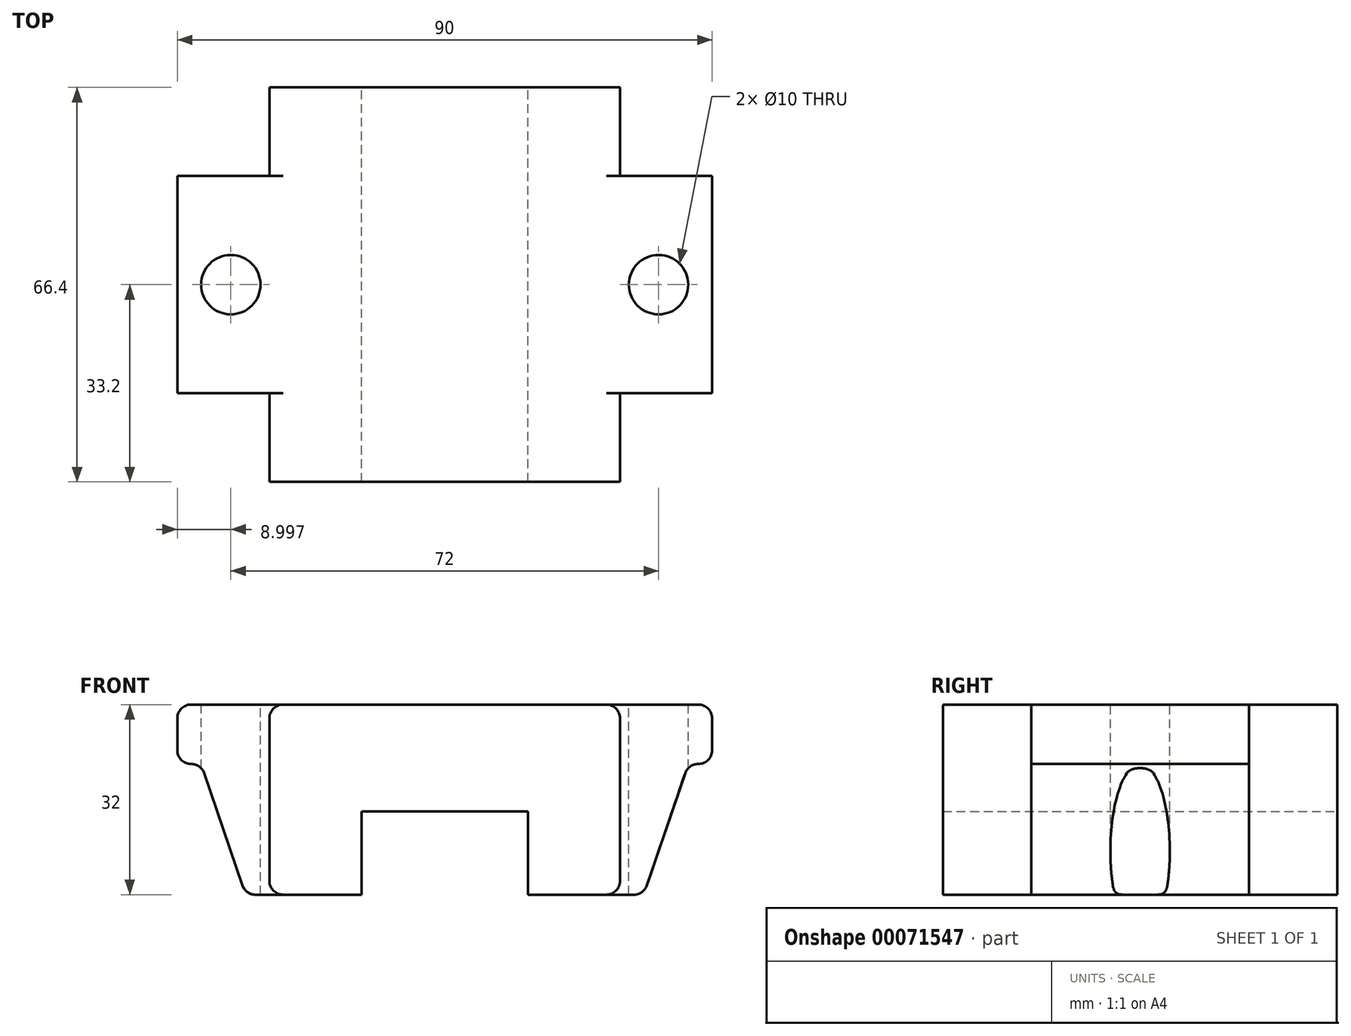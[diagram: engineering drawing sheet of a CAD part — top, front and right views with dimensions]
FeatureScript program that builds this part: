
annotation { "Feature Type Name" : "Feature", "Feature Type Description" : "" }
export const myFeature = defineFeature(function(context is Context, id is Id, definition is map)
    precondition{}
    {
        {
            var Q0;
            Q0=qCreatedBy(makeId("Front.planeOp"),FACE);
            var sketch = newSketch(context, id + "F0", { "sketchPlane" : qUnion([Q0])});
            skLineSegment(sketch, "E0.bottom", {"start": v(-43.91, 8.76) * mm, "end": v(46.09, 8.76) * mm});
            skLineSegment(sketch, "E0.top", {"start": v(-32.41, -23.24) * mm, "end": v(-12.91, -23.24) * mm});
            skLineSegment(sketch, "E0.left", {"start": v(-43.91, 8.76) * mm, "end": v(-43.91, -1.24) * mm});
            skLineSegment(sketch, "E0.right", {"start": v(46.09, 8.76) * mm, "end": v(46.09, -1.24) * mm});
            skLineSegment(sketch, "E1.top", {"start": v(-43.91, -1.24) * mm, "end": v(-39.91, -1.24) * mm});
            skLineSegment(sketch, "E2.bottom", {"start": v(-28.41, 8.76) * mm, "end": v(30.59, 8.76) * mm});
            skLineSegment(sketch, "E2.top", {"start": v(-28.41, -23.24) * mm, "end": v(-12.91, -23.24) * mm});
            skLineSegment(sketch, "E2.left", {"start": v(-28.41, 8.76) * mm, "end": v(-28.41, -23.24) * mm});
            skLineSegment(sketch, "E2.right", {"start": v(30.59, 8.76) * mm, "end": v(30.59, -23.24) * mm});
            skLineSegment(sketch, "E3.top", {"start": v(-12.91, -9.24) * mm, "end": v(15.09, -9.24) * mm});
            skLineSegment(sketch, "E3.left", {"start": v(-12.91, -23.24) * mm, "end": v(-12.91, -9.24) * mm});
            skLineSegment(sketch, "E3.right", {"start": v(15.09, -23.24) * mm, "end": v(15.09, -9.24) * mm});
            skLineSegment(sketch, "E4.trimOffspring", {"start": v(15.09, -23.24) * mm, "end": v(30.59, -23.24) * mm});
            skLineSegment(sketch, "E5.trimOffspring", {"start": v(15.09, -23.24) * mm, "end": v(34.59, -23.24) * mm});
            skLineSegment(sketch, "E6", {"start": v(-39.91, -1.24) * mm, "end": v(-32.41, -23.24) * mm});
            skLineSegment(sketch, "E7", {"start": v(34.59, -23.24) * mm, "end": v(42.09, -1.24) * mm});
            skLineSegment(sketch, "E8.trimOffspring", {"start": v(42.09, -1.24) * mm, "end": v(46.09, -1.24) * mm});
            skSolve(sketch);
        }
        {
            var Q0;
            Q0=qSketchRegion(id+"F0",true);
            extrude(context, id + "F1", {"entities" : qUnion([Q0]), "depth" : 36.6 * mm});
        }
        {
            var Q0;
            Q0=makeQuery(id+"F1.opExtrude","CAP_FACE",FACE,{"disambiguationData":[OSD([sQuery(id+"F0.wireOp",EDGE,"E0.top"),sQuery(id+"F0.wireOp",EDGE,"E0.bottom"),sQuery(id+"F0.wireOp",EDGE,"E1.top"),sQuery(id+"F0.wireOp",EDGE,"E0.left"),sQuery(id+"F0.wireOp",EDGE,"E0.right"),sQuery(id+"F0.wireOp",EDGE,"E2.bottom"),sQuery(id+"F0.wireOp",EDGE,"E2.top"),sQuery(id+"F0.wireOp",EDGE,"E3.top"),sQuery(id+"F0.wireOp",EDGE,"E3.left"),sQuery(id+"F0.wireOp",EDGE,"E3.right"),sQuery(id+"F0.wireOp",EDGE,"E5.trimOffspring"),sQuery(id+"F0.wireOp",EDGE,"E6"),sQuery(id+"F0.wireOp",EDGE,"E7"),sQuery(id+"F0.wireOp",EDGE,"E8.trimOffspring")])],"isStart":true});
            var sketch = newSketch(context, id + "F2", { "sketchPlane" : qUnion([Q0])});
            skLineSegment(sketch, "E9.top", {"start": v(-30.59, 8.76) * mm, "end": v(28.41, 8.76) * mm});
            skLineSegment(sketch, "E9.left", {"start": v(-30.59, -23.24) * mm, "end": v(-30.59, 8.76) * mm});
            skLineSegment(sketch, "E9.right", {"start": v(28.41, -23.24) * mm, "end": v(28.41, 8.76) * mm});
            skLineSegment(sketch, "E10.top", {"start": v(-15.09, -9.24) * mm, "end": v(12.91, -9.24) * mm});
            skLineSegment(sketch, "E10.left", {"start": v(-15.09, -23.24) * mm, "end": v(-15.09, -9.24) * mm});
            skLineSegment(sketch, "E10.right", {"start": v(12.91, -23.24) * mm, "end": v(12.91, -9.24) * mm});
            skLineSegment(sketch, "E11.trimOffspring", {"start": v(12.91, -23.24) * mm, "end": v(28.41, -23.24) * mm});
            skLineSegment(sketch, "E12", {"start": v(-30.59, -23.24) * mm, "end": v(-15.09, -23.24) * mm});
            skSolve(sketch);
        }
        {
            var Q0;
            Q0=qSketchRegion(id+"F2",true);
            extrude(context, id + "F3", {"entities" : qUnion([Q0]), "operationType" : NewBodyOperationType.ADD, "depth" : 14.9 * mm, "hasSecondDirection" : true, "secondDirectionOppositeDirection" : true, "secondDirectionDepth" : 51.5 * mm});
        }
        {
            var Q0;
            Q0=makeQuery(id+"F3.boolean.opBoolean","MERGE",FACE,{"derivedFrom":[makeQuery(id+"F1.opExtrude","SWEPT_FACE",FACE,{"disambiguationData":[OSD([sQuery(id+"F0.wireOp",EDGE,"E0.bottom"),sQuery(id+"F0.wireOp",EDGE,"E2.bottom")])]}),makeQuery(id+"F3.opExtrude","SWEPT_FACE",FACE,{"disambiguationData":[OSD([sQuery(id+"F2.wireOp",EDGE,"E9.top")])]})]});
            var sketch = newSketch(context, id + "F4", { "sketchPlane" : qUnion([Q0])});
            skCircle(sketch, "E13", {"center": v(-34.91, -18.3) * mm, "radius": 5 * mm});
            skCircle(sketch, "E14", {"center": v(37.09, -18.3) * mm, "radius": 5 * mm});
            skSolve(sketch);
        }
        {
            var Q0;
            Q0=qSketchRegion(id+"F4",true);
            extrude(context, id + "F5", {"entities" : qUnion([Q0]), "operationType" : NewBodyOperationType.REMOVE, "endBound" : BoundingType.THROUGH_ALL, "oppositeDirection" : true, "depth" : 25 * mm});
        }
        {
            var Q0;
            {var subQ0=sQuery(id+"F0.wireOp",EDGE,"E6");var subQ1=sQuery(id+"F0.wireOp",EDGE,"E1.top");Q0=makeQuery(id+"F5.boolean.opBoolean","SPLIT",EDGE,{"disambiguationData":[TD([makeQuery(id+"F1.opExtrude","CAP_FACE",FACE,{"disambiguationData":[OSD([sQuery(id+"F0.wireOp",EDGE,"E0.top"),sQuery(id+"F0.wireOp",EDGE,"E0.bottom"),subQ1,sQuery(id+"F0.wireOp",EDGE,"E0.left"),sQuery(id+"F0.wireOp",EDGE,"E0.right"),sQuery(id+"F0.wireOp",EDGE,"E2.bottom"),sQuery(id+"F0.wireOp",EDGE,"E2.top"),sQuery(id+"F0.wireOp",EDGE,"E3.top"),sQuery(id+"F0.wireOp",EDGE,"E3.left"),sQuery(id+"F0.wireOp",EDGE,"E3.right"),sQuery(id+"F0.wireOp",EDGE,"E5.trimOffspring"),subQ0,sQuery(id+"F0.wireOp",EDGE,"E7"),sQuery(id+"F0.wireOp",EDGE,"E8.trimOffspring")])],"isStart":false})])],"derivedFrom":makeQuery(id+"F1.opExtrude","SWEPT_EDGE",EDGE,{"disambiguationData":[OSD([subQ1,subQ0])]})});}
            var Q1;
            Q1=makeQuery(id+"F1.opExtrude","SWEPT_EDGE",EDGE,{"disambiguationData":[OSD([sQuery(id+"F0.wireOp",EDGE,"E1.top"),sQuery(id+"F0.wireOp",EDGE,"E0.left")])]});
            var Q2;
            Q2=makeQuery(id+"F1.opExtrude","SWEPT_EDGE",EDGE,{"disambiguationData":[OSD([sQuery(id+"F0.wireOp",EDGE,"E0.bottom"),sQuery(id+"F0.wireOp",EDGE,"E0.left")])]});
            var Q3;
            {var subQ0=sQuery(id+"F0.wireOp",EDGE,"E6");var subQ1=sQuery(id+"F0.wireOp",EDGE,"E2.top");var subQ2=sQuery(id+"F0.wireOp",EDGE,"E0.top");Q3=makeQuery(id+"F5.boolean.opBoolean","SPLIT",EDGE,{"disambiguationData":[TD([makeQuery(id+"F1.opExtrude","CAP_FACE",FACE,{"disambiguationData":[OSD([subQ2,sQuery(id+"F0.wireOp",EDGE,"E0.bottom"),sQuery(id+"F0.wireOp",EDGE,"E1.top"),sQuery(id+"F0.wireOp",EDGE,"E0.left"),sQuery(id+"F0.wireOp",EDGE,"E0.right"),sQuery(id+"F0.wireOp",EDGE,"E2.bottom"),subQ1,sQuery(id+"F0.wireOp",EDGE,"E3.top"),sQuery(id+"F0.wireOp",EDGE,"E3.left"),sQuery(id+"F0.wireOp",EDGE,"E3.right"),sQuery(id+"F0.wireOp",EDGE,"E5.trimOffspring"),subQ0,sQuery(id+"F0.wireOp",EDGE,"E7"),sQuery(id+"F0.wireOp",EDGE,"E8.trimOffspring")])],"isStart":false})])],"derivedFrom":makeQuery(id+"F1.opExtrude","SWEPT_EDGE",EDGE,{"disambiguationData":[OSD([subQ2,subQ0])]})});}
            var Q4;
            {var subQ0=sQuery(id+"F0.wireOp",EDGE,"E6");var subQ1=sQuery(id+"F0.wireOp",EDGE,"E2.top");var subQ2=sQuery(id+"F0.wireOp",EDGE,"E0.top");Q4=makeQuery(id+"F5.boolean.opBoolean","SPLIT",EDGE,{"disambiguationData":[TD([makeQuery(id+"F1.opExtrude","CAP_FACE",FACE,{"disambiguationData":[OSD([subQ2,sQuery(id+"F0.wireOp",EDGE,"E0.bottom"),sQuery(id+"F0.wireOp",EDGE,"E1.top"),sQuery(id+"F0.wireOp",EDGE,"E0.left"),sQuery(id+"F0.wireOp",EDGE,"E0.right"),sQuery(id+"F0.wireOp",EDGE,"E2.bottom"),subQ1,sQuery(id+"F0.wireOp",EDGE,"E3.top"),sQuery(id+"F0.wireOp",EDGE,"E3.left"),sQuery(id+"F0.wireOp",EDGE,"E3.right"),sQuery(id+"F0.wireOp",EDGE,"E5.trimOffspring"),subQ0,sQuery(id+"F0.wireOp",EDGE,"E7"),sQuery(id+"F0.wireOp",EDGE,"E8.trimOffspring")])],"isStart":true})])],"derivedFrom":makeQuery(id+"F1.opExtrude","SWEPT_EDGE",EDGE,{"disambiguationData":[OSD([subQ2,subQ0])]})});}
            var Q5;
            {var subQ0=sQuery(id+"F2.wireOp",EDGE,"E9.right");var subQ1=sQuery(id+"F0.wireOp",EDGE,"E2.top");var subQ2=sQuery(id+"F0.wireOp",EDGE,"E0.top");var subQ3=sQuery(id+"F2.wireOp",EDGE,"E11.trimOffspring");Q5=makeQuery(id+"F3.boolean.opBoolean","SPLIT",EDGE,{"disambiguationData":[TD([makeQuery(id+"F3.opExtrude","CAP_FACE",FACE,{"disambiguationData":[OSD([sQuery(id+"F2.wireOp",EDGE,"E9.top"),sQuery(id+"F2.wireOp",EDGE,"E9.left"),subQ0,sQuery(id+"F2.wireOp",EDGE,"E10.top"),sQuery(id+"F2.wireOp",EDGE,"E10.left"),sQuery(id+"F2.wireOp",EDGE,"E10.right"),subQ3,sQuery(id+"F2.wireOp",EDGE,"E12")])],"isStart":true})])],"derivedFrom":makeQuery(id+"F3.opExtrude","SWEPT_EDGE",EDGE,{"disambiguationData":[OSD([subQ2,subQ1,subQ0,subQ3])]})});}
            var Q6;
            {var subQ0=sQuery(id+"F2.wireOp",EDGE,"E9.right");var subQ1=sQuery(id+"F0.wireOp",EDGE,"E2.top");var subQ2=sQuery(id+"F0.wireOp",EDGE,"E0.top");var subQ3=sQuery(id+"F2.wireOp",EDGE,"E11.trimOffspring");Q6=makeQuery(id+"F3.boolean.opBoolean","SPLIT",EDGE,{"disambiguationData":[TD([makeQuery(id+"F3.opExtrude","CAP_FACE",FACE,{"disambiguationData":[OSD([sQuery(id+"F2.wireOp",EDGE,"E9.top"),sQuery(id+"F2.wireOp",EDGE,"E9.left"),subQ0,sQuery(id+"F2.wireOp",EDGE,"E10.top"),sQuery(id+"F2.wireOp",EDGE,"E10.left"),sQuery(id+"F2.wireOp",EDGE,"E10.right"),subQ3,sQuery(id+"F2.wireOp",EDGE,"E12")])],"isStart":false})])],"derivedFrom":makeQuery(id+"F3.opExtrude","SWEPT_EDGE",EDGE,{"disambiguationData":[OSD([subQ2,subQ1,subQ0,subQ3])]})});}
            var Q7;
            {var subQ0=sQuery(id+"F0.wireOp",EDGE,"E2.bottom");var subQ1=sQuery(id+"F0.wireOp",EDGE,"E0.bottom");var subQ2=sQuery(id+"F2.wireOp",EDGE,"E9.right");var subQ3=sQuery(id+"F2.wireOp",EDGE,"E9.top");Q7=makeQuery(id+"F3.boolean.opBoolean","SPLIT",EDGE,{"disambiguationData":[TD([makeQuery(id+"F3.opExtrude","CAP_FACE",FACE,{"disambiguationData":[OSD([subQ3,sQuery(id+"F2.wireOp",EDGE,"E9.left"),subQ2,sQuery(id+"F2.wireOp",EDGE,"E10.top"),sQuery(id+"F2.wireOp",EDGE,"E10.left"),sQuery(id+"F2.wireOp",EDGE,"E10.right"),sQuery(id+"F2.wireOp",EDGE,"E11.trimOffspring"),sQuery(id+"F2.wireOp",EDGE,"E12")])],"isStart":true})])],"derivedFrom":makeQuery(id+"F3.opExtrude","SWEPT_EDGE",EDGE,{"disambiguationData":[OSD([subQ1,subQ0,subQ3,subQ2])]})});}
            var Q8;
            {var subQ0=sQuery(id+"F0.wireOp",EDGE,"E2.bottom");var subQ1=sQuery(id+"F0.wireOp",EDGE,"E0.bottom");var subQ2=sQuery(id+"F2.wireOp",EDGE,"E9.right");var subQ3=sQuery(id+"F2.wireOp",EDGE,"E9.top");Q8=makeQuery(id+"F3.boolean.opBoolean","SPLIT",EDGE,{"disambiguationData":[TD([makeQuery(id+"F3.opExtrude","CAP_FACE",FACE,{"disambiguationData":[OSD([subQ3,sQuery(id+"F2.wireOp",EDGE,"E9.left"),subQ2,sQuery(id+"F2.wireOp",EDGE,"E10.top"),sQuery(id+"F2.wireOp",EDGE,"E10.left"),sQuery(id+"F2.wireOp",EDGE,"E10.right"),sQuery(id+"F2.wireOp",EDGE,"E11.trimOffspring"),sQuery(id+"F2.wireOp",EDGE,"E12")])],"isStart":false})])],"derivedFrom":makeQuery(id+"F3.opExtrude","SWEPT_EDGE",EDGE,{"disambiguationData":[OSD([subQ1,subQ0,subQ3,subQ2])]})});}
            var Q9;
            {var subQ0=sQuery(id+"F0.wireOp",EDGE,"E2.bottom");var subQ1=sQuery(id+"F0.wireOp",EDGE,"E0.bottom");var subQ2=sQuery(id+"F2.wireOp",EDGE,"E9.left");var subQ3=sQuery(id+"F2.wireOp",EDGE,"E9.top");Q9=makeQuery(id+"F3.boolean.opBoolean","SPLIT",EDGE,{"disambiguationData":[TD([makeQuery(id+"F3.opExtrude","CAP_FACE",FACE,{"disambiguationData":[OSD([subQ3,subQ2,sQuery(id+"F2.wireOp",EDGE,"E9.right"),sQuery(id+"F2.wireOp",EDGE,"E10.top"),sQuery(id+"F2.wireOp",EDGE,"E10.left"),sQuery(id+"F2.wireOp",EDGE,"E10.right"),sQuery(id+"F2.wireOp",EDGE,"E11.trimOffspring"),sQuery(id+"F2.wireOp",EDGE,"E12")])],"isStart":false})])],"derivedFrom":makeQuery(id+"F3.opExtrude","SWEPT_EDGE",EDGE,{"disambiguationData":[OSD([subQ1,subQ0,subQ3,subQ2])]})});}
            var Q10;
            {var subQ0=sQuery(id+"F0.wireOp",EDGE,"E2.bottom");var subQ1=sQuery(id+"F0.wireOp",EDGE,"E0.bottom");var subQ2=sQuery(id+"F2.wireOp",EDGE,"E9.left");var subQ3=sQuery(id+"F2.wireOp",EDGE,"E9.top");Q10=makeQuery(id+"F3.boolean.opBoolean","SPLIT",EDGE,{"disambiguationData":[TD([makeQuery(id+"F3.opExtrude","CAP_FACE",FACE,{"disambiguationData":[OSD([subQ3,subQ2,sQuery(id+"F2.wireOp",EDGE,"E9.right"),sQuery(id+"F2.wireOp",EDGE,"E10.top"),sQuery(id+"F2.wireOp",EDGE,"E10.left"),sQuery(id+"F2.wireOp",EDGE,"E10.right"),sQuery(id+"F2.wireOp",EDGE,"E11.trimOffspring"),sQuery(id+"F2.wireOp",EDGE,"E12")])],"isStart":true})])],"derivedFrom":makeQuery(id+"F3.opExtrude","SWEPT_EDGE",EDGE,{"disambiguationData":[OSD([subQ1,subQ0,subQ3,subQ2])]})});}
            var Q11;
            Q11=makeQuery(id+"F1.opExtrude","SWEPT_EDGE",EDGE,{"disambiguationData":[OSD([sQuery(id+"F0.wireOp",EDGE,"E0.bottom"),sQuery(id+"F0.wireOp",EDGE,"E0.right")])]});
            var Q12;
            Q12=makeQuery(id+"F1.opExtrude","SWEPT_EDGE",EDGE,{"disambiguationData":[OSD([sQuery(id+"F0.wireOp",EDGE,"E0.right"),sQuery(id+"F0.wireOp",EDGE,"E8.trimOffspring")])]});
            var Q13;
            {var subQ0=sQuery(id+"F0.wireOp",EDGE,"E8.trimOffspring");var subQ1=sQuery(id+"F0.wireOp",EDGE,"E7");Q13=makeQuery(id+"F5.boolean.opBoolean","SPLIT",EDGE,{"disambiguationData":[TD([makeQuery(id+"F1.opExtrude","CAP_FACE",FACE,{"disambiguationData":[OSD([sQuery(id+"F0.wireOp",EDGE,"E0.top"),sQuery(id+"F0.wireOp",EDGE,"E0.bottom"),sQuery(id+"F0.wireOp",EDGE,"E1.top"),sQuery(id+"F0.wireOp",EDGE,"E0.left"),sQuery(id+"F0.wireOp",EDGE,"E0.right"),sQuery(id+"F0.wireOp",EDGE,"E2.bottom"),sQuery(id+"F0.wireOp",EDGE,"E2.top"),sQuery(id+"F0.wireOp",EDGE,"E3.top"),sQuery(id+"F0.wireOp",EDGE,"E3.left"),sQuery(id+"F0.wireOp",EDGE,"E3.right"),sQuery(id+"F0.wireOp",EDGE,"E5.trimOffspring"),sQuery(id+"F0.wireOp",EDGE,"E6"),subQ1,subQ0])],"isStart":false})])],"derivedFrom":makeQuery(id+"F1.opExtrude","SWEPT_EDGE",EDGE,{"disambiguationData":[OSD([subQ1,subQ0])]})});}
            var Q14;
            {var subQ0=sQuery(id+"F0.wireOp",EDGE,"E7");var subQ1=sQuery(id+"F0.wireOp",EDGE,"E5.trimOffspring");Q14=makeQuery(id+"F5.boolean.opBoolean","SPLIT",EDGE,{"disambiguationData":[TD([makeQuery(id+"F1.opExtrude","CAP_FACE",FACE,{"disambiguationData":[OSD([sQuery(id+"F0.wireOp",EDGE,"E0.top"),sQuery(id+"F0.wireOp",EDGE,"E0.bottom"),sQuery(id+"F0.wireOp",EDGE,"E1.top"),sQuery(id+"F0.wireOp",EDGE,"E0.left"),sQuery(id+"F0.wireOp",EDGE,"E0.right"),sQuery(id+"F0.wireOp",EDGE,"E2.bottom"),sQuery(id+"F0.wireOp",EDGE,"E2.top"),sQuery(id+"F0.wireOp",EDGE,"E3.top"),sQuery(id+"F0.wireOp",EDGE,"E3.left"),sQuery(id+"F0.wireOp",EDGE,"E3.right"),subQ1,sQuery(id+"F0.wireOp",EDGE,"E6"),subQ0,sQuery(id+"F0.wireOp",EDGE,"E8.trimOffspring")])],"isStart":false})])],"derivedFrom":makeQuery(id+"F1.opExtrude","SWEPT_EDGE",EDGE,{"disambiguationData":[OSD([subQ1,subQ0])]})});}
            var Q15;
            {var subQ0=sQuery(id+"F0.wireOp",EDGE,"E7");var subQ1=sQuery(id+"F0.wireOp",EDGE,"E5.trimOffspring");Q15=makeQuery(id+"F5.boolean.opBoolean","SPLIT",EDGE,{"disambiguationData":[TD([makeQuery(id+"F1.opExtrude","CAP_FACE",FACE,{"disambiguationData":[OSD([sQuery(id+"F0.wireOp",EDGE,"E0.top"),sQuery(id+"F0.wireOp",EDGE,"E0.bottom"),sQuery(id+"F0.wireOp",EDGE,"E1.top"),sQuery(id+"F0.wireOp",EDGE,"E0.left"),sQuery(id+"F0.wireOp",EDGE,"E0.right"),sQuery(id+"F0.wireOp",EDGE,"E2.bottom"),sQuery(id+"F0.wireOp",EDGE,"E2.top"),sQuery(id+"F0.wireOp",EDGE,"E3.top"),sQuery(id+"F0.wireOp",EDGE,"E3.left"),sQuery(id+"F0.wireOp",EDGE,"E3.right"),subQ1,sQuery(id+"F0.wireOp",EDGE,"E6"),subQ0,sQuery(id+"F0.wireOp",EDGE,"E8.trimOffspring")])],"isStart":true})])],"derivedFrom":makeQuery(id+"F1.opExtrude","SWEPT_EDGE",EDGE,{"disambiguationData":[OSD([subQ1,subQ0])]})});}
            var Q16;
            {var subQ0=sQuery(id+"F0.wireOp",EDGE,"E5.trimOffspring");var subQ1=sQuery(id+"F2.wireOp",EDGE,"E12");var subQ2=sQuery(id+"F2.wireOp",EDGE,"E9.left");Q16=makeQuery(id+"F3.boolean.opBoolean","SPLIT",EDGE,{"disambiguationData":[TD([makeQuery(id+"F3.opExtrude","CAP_FACE",FACE,{"disambiguationData":[OSD([sQuery(id+"F2.wireOp",EDGE,"E9.top"),subQ2,sQuery(id+"F2.wireOp",EDGE,"E9.right"),sQuery(id+"F2.wireOp",EDGE,"E10.top"),sQuery(id+"F2.wireOp",EDGE,"E10.left"),sQuery(id+"F2.wireOp",EDGE,"E10.right"),sQuery(id+"F2.wireOp",EDGE,"E11.trimOffspring"),subQ1])],"isStart":true})])],"derivedFrom":makeQuery(id+"F3.opExtrude","SWEPT_EDGE",EDGE,{"disambiguationData":[OSD([subQ0,subQ2,subQ1])]})});}
            var Q17;
            {var subQ0=sQuery(id+"F0.wireOp",EDGE,"E5.trimOffspring");var subQ1=sQuery(id+"F2.wireOp",EDGE,"E12");var subQ2=sQuery(id+"F2.wireOp",EDGE,"E9.left");Q17=makeQuery(id+"F3.boolean.opBoolean","SPLIT",EDGE,{"disambiguationData":[TD([makeQuery(id+"F3.opExtrude","CAP_FACE",FACE,{"disambiguationData":[OSD([sQuery(id+"F2.wireOp",EDGE,"E9.top"),subQ2,sQuery(id+"F2.wireOp",EDGE,"E9.right"),sQuery(id+"F2.wireOp",EDGE,"E10.top"),sQuery(id+"F2.wireOp",EDGE,"E10.left"),sQuery(id+"F2.wireOp",EDGE,"E10.right"),sQuery(id+"F2.wireOp",EDGE,"E11.trimOffspring"),subQ1])],"isStart":false})])],"derivedFrom":makeQuery(id+"F3.opExtrude","SWEPT_EDGE",EDGE,{"disambiguationData":[OSD([subQ0,subQ2,subQ1])]})});}
            var Q18;
            {var subQ0=sQuery(id+"F0.wireOp",EDGE,"E8.trimOffspring");var subQ1=sQuery(id+"F0.wireOp",EDGE,"E7");Q18=makeQuery(id+"F5.boolean.opBoolean","SPLIT",EDGE,{"disambiguationData":[TD([makeQuery(id+"F1.opExtrude","CAP_FACE",FACE,{"disambiguationData":[OSD([sQuery(id+"F0.wireOp",EDGE,"E0.top"),sQuery(id+"F0.wireOp",EDGE,"E0.bottom"),sQuery(id+"F0.wireOp",EDGE,"E1.top"),sQuery(id+"F0.wireOp",EDGE,"E0.left"),sQuery(id+"F0.wireOp",EDGE,"E0.right"),sQuery(id+"F0.wireOp",EDGE,"E2.bottom"),sQuery(id+"F0.wireOp",EDGE,"E2.top"),sQuery(id+"F0.wireOp",EDGE,"E3.top"),sQuery(id+"F0.wireOp",EDGE,"E3.left"),sQuery(id+"F0.wireOp",EDGE,"E3.right"),sQuery(id+"F0.wireOp",EDGE,"E5.trimOffspring"),sQuery(id+"F0.wireOp",EDGE,"E6"),subQ1,subQ0])],"isStart":true})])],"derivedFrom":makeQuery(id+"F1.opExtrude","SWEPT_EDGE",EDGE,{"disambiguationData":[OSD([subQ1,subQ0])]})});}
            var Q19;
            {var subQ0=sQuery(id+"F0.wireOp",EDGE,"E6");var subQ1=sQuery(id+"F0.wireOp",EDGE,"E1.top");Q19=makeQuery(id+"F5.boolean.opBoolean","SPLIT",EDGE,{"disambiguationData":[TD([makeQuery(id+"F1.opExtrude","CAP_FACE",FACE,{"disambiguationData":[OSD([sQuery(id+"F0.wireOp",EDGE,"E0.top"),sQuery(id+"F0.wireOp",EDGE,"E0.bottom"),subQ1,sQuery(id+"F0.wireOp",EDGE,"E0.left"),sQuery(id+"F0.wireOp",EDGE,"E0.right"),sQuery(id+"F0.wireOp",EDGE,"E2.bottom"),sQuery(id+"F0.wireOp",EDGE,"E2.top"),sQuery(id+"F0.wireOp",EDGE,"E3.top"),sQuery(id+"F0.wireOp",EDGE,"E3.left"),sQuery(id+"F0.wireOp",EDGE,"E3.right"),sQuery(id+"F0.wireOp",EDGE,"E5.trimOffspring"),subQ0,sQuery(id+"F0.wireOp",EDGE,"E7"),sQuery(id+"F0.wireOp",EDGE,"E8.trimOffspring")])],"isStart":true})])],"derivedFrom":makeQuery(id+"F1.opExtrude","SWEPT_EDGE",EDGE,{"disambiguationData":[OSD([subQ1,subQ0])]})});}
            fillet(context, id + "F6", {"entities" : qUnion([Q0, Q1, Q2, Q3, Q4, Q5, Q6, Q7, Q8, Q9, Q10, Q11, Q12, Q13, Q14, Q15, Q16, Q17, Q18, Q19]), "radius" : 2.3 * mm, "tangentPropagation" : true, "allowEdgeOverflow" : false});
        }
    });
